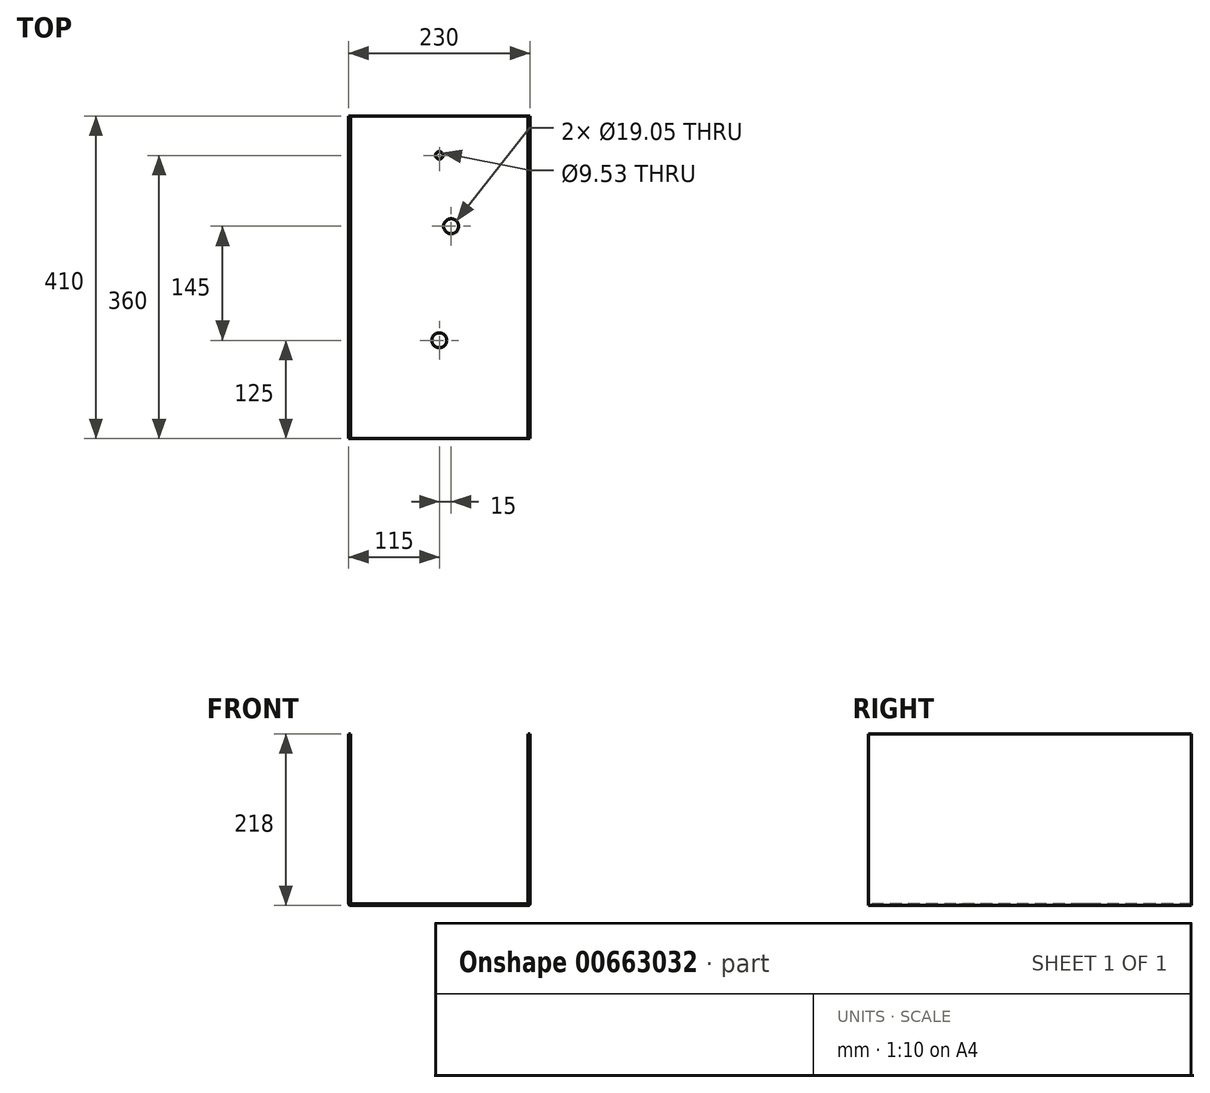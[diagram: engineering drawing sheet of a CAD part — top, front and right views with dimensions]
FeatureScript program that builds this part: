
annotation { "Feature Type Name" : "Feature", "Feature Type Description" : "" }
export const myFeature = defineFeature(function(context is Context, id is Id, definition is map)
    precondition{}
    {
        {
            var Q0;
            Q0=qCreatedBy(makeId("Front.planeOp"),FACE);
            var sketch = newSketch(context, id + "F0", { "sketchPlane" : qUnion([Q0])});
            skLineSegment(sketch, "E0", {"start": v(2, 0) * mm, "end": v(228, 0) * mm});
            skLineSegment(sketch, "E1", {"start": v(230, 2) * mm, "end": v(230, 218) * mm});
            skLineSegment(sketch, "E2", {"start": v(0, 2) * mm, "end": v(0, 218) * mm});
            skLineSegment(sketch, "E3.0", {"start": v(2, 2) * mm, "end": v(2, 218) * mm});
            skLineSegment(sketch, "E3.1", {"start": v(2, 2) * mm, "end": v(228, 2) * mm});
            skLineSegment(sketch, "E3.2", {"start": v(228, 2) * mm, "end": v(228, 218) * mm});
            skLineSegment(sketch, "E4", {"start": v(0, 218) * mm, "end": v(2, 218) * mm});
            skLineSegment(sketch, "E5", {"start": v(228, 218) * mm, "end": v(230, 218) * mm});
            skPoint(sketch, "E6.visualSharp", {"position": v(0, 0) * mm});
            skArc(sketch, "E6.filletArc", {"start": v(0, 2) * mm, "mid": v(0.59, 0.59) * mm, "end": v(2, 0) * mm});
            skPoint(sketch, "E7.visualSharp", {"position": v(230, 0) * mm});
            skArc(sketch, "E7.filletArc", {"start": v(228, 0) * mm, "mid": v(229.41, 0.59) * mm, "end": v(230, 2) * mm});
            skSolve(sketch);
        }
        {
            var Q0;
            Q0=makeQuery(id+"F0.imprint","IMPRINT",FACE,{"disambiguationData":[TD([[makeQuery(id+"F0.imprint","IMPRINT",EDGE,{"derivedFrom":sQuery(id+"F0.wireOp",EDGE,"E0")}),1.0]])]});
            extrude(context, id + "F1", {"entities" : qUnion([Q0]), "oppositeDirection" : true, "depth" : 410 * mm, "offsetDistance" : 25 * mm});
        }
        {
            var Q0;
            Q0=makeQuery(id+"F1.opExtrude","SWEPT_FACE",FACE,{"disambiguationData":[OSD([sQuery(id+"F0.wireOp",EDGE,"E3.1")])]});
            var sketch = newSketch(context, id + "F2", { "sketchPlane" : qUnion([Q0])});
            skPoint(sketch, "E8", {"position": v(115, 125) * mm});
            skPoint(sketch, "E9", {"position": v(115, 360) * mm});
            skPoint(sketch, "E10", {"position": v(130, 270) * mm});
            skSolve(sketch);
        }
        {
            var Q0;
            Q0=sQuery(id+"F2.wireOp",VERTEX,"E8");
            var Q1;
            Q1=sQuery(id+"F2.wireOp",VERTEX,"E10");
            var Q2;
            Q2=makeQuery(id+"F1.opExtrude","SWEPT_BODY",BODY,{"disambiguationData":[OSD([sQuery(id+"F0.wireOp",EDGE,"E0"),sQuery(id+"F0.wireOp",EDGE,"E1"),sQuery(id+"F0.wireOp",EDGE,"E2"),sQuery(id+"F0.wireOp",EDGE,"E3.0"),sQuery(id+"F0.wireOp",EDGE,"E3.1"),sQuery(id+"F0.wireOp",EDGE,"E3.2"),sQuery(id+"F0.wireOp",EDGE,"E4"),sQuery(id+"F0.wireOp",EDGE,"E5"),sQuery(id+"F0.wireOp",EDGE,"E6.filletArc"),sQuery(id+"F0.wireOp",EDGE,"E7.filletArc")])]});
            hole(context, id + "F3", {"style" : HoleStyle.SIMPLE, "endStyle" : HoleEndStyle.BLIND, "holeDiameter" : 19.05 * mm, "majorDiameter" : 5 * mm, "holeDepth" : 5 * mm, "isTappedThrough" : true, "tappedDepth" : 12 * mm, "tapClearance" : 3, "locations" : qUnion([Q0, Q1]), "scope" : qUnion([Q2])});
        }
        {
            var Q0;
            Q0=sQuery(id+"F2.wireOp",VERTEX,"E9");
            var Q1;
            Q1=makeQuery(id+"F1.opExtrude","SWEPT_BODY",BODY,{"disambiguationData":[OSD([sQuery(id+"F0.wireOp",EDGE,"E0"),sQuery(id+"F0.wireOp",EDGE,"E1"),sQuery(id+"F0.wireOp",EDGE,"E2"),sQuery(id+"F0.wireOp",EDGE,"E3.0"),sQuery(id+"F0.wireOp",EDGE,"E3.1"),sQuery(id+"F0.wireOp",EDGE,"E3.2"),sQuery(id+"F0.wireOp",EDGE,"E4"),sQuery(id+"F0.wireOp",EDGE,"E5"),sQuery(id+"F0.wireOp",EDGE,"E6.filletArc"),sQuery(id+"F0.wireOp",EDGE,"E7.filletArc")])]});
            hole(context, id + "F4", {"style" : HoleStyle.SIMPLE, "endStyle" : HoleEndStyle.BLIND, "holeDiameter" : 9.53 * mm, "majorDiameter" : 5 * mm, "holeDepth" : 5 * mm, "isTappedThrough" : true, "tappedDepth" : 12 * mm, "tapClearance" : 3, "locations" : qUnion([Q0]), "scope" : qUnion([Q1])});
        }
    });
